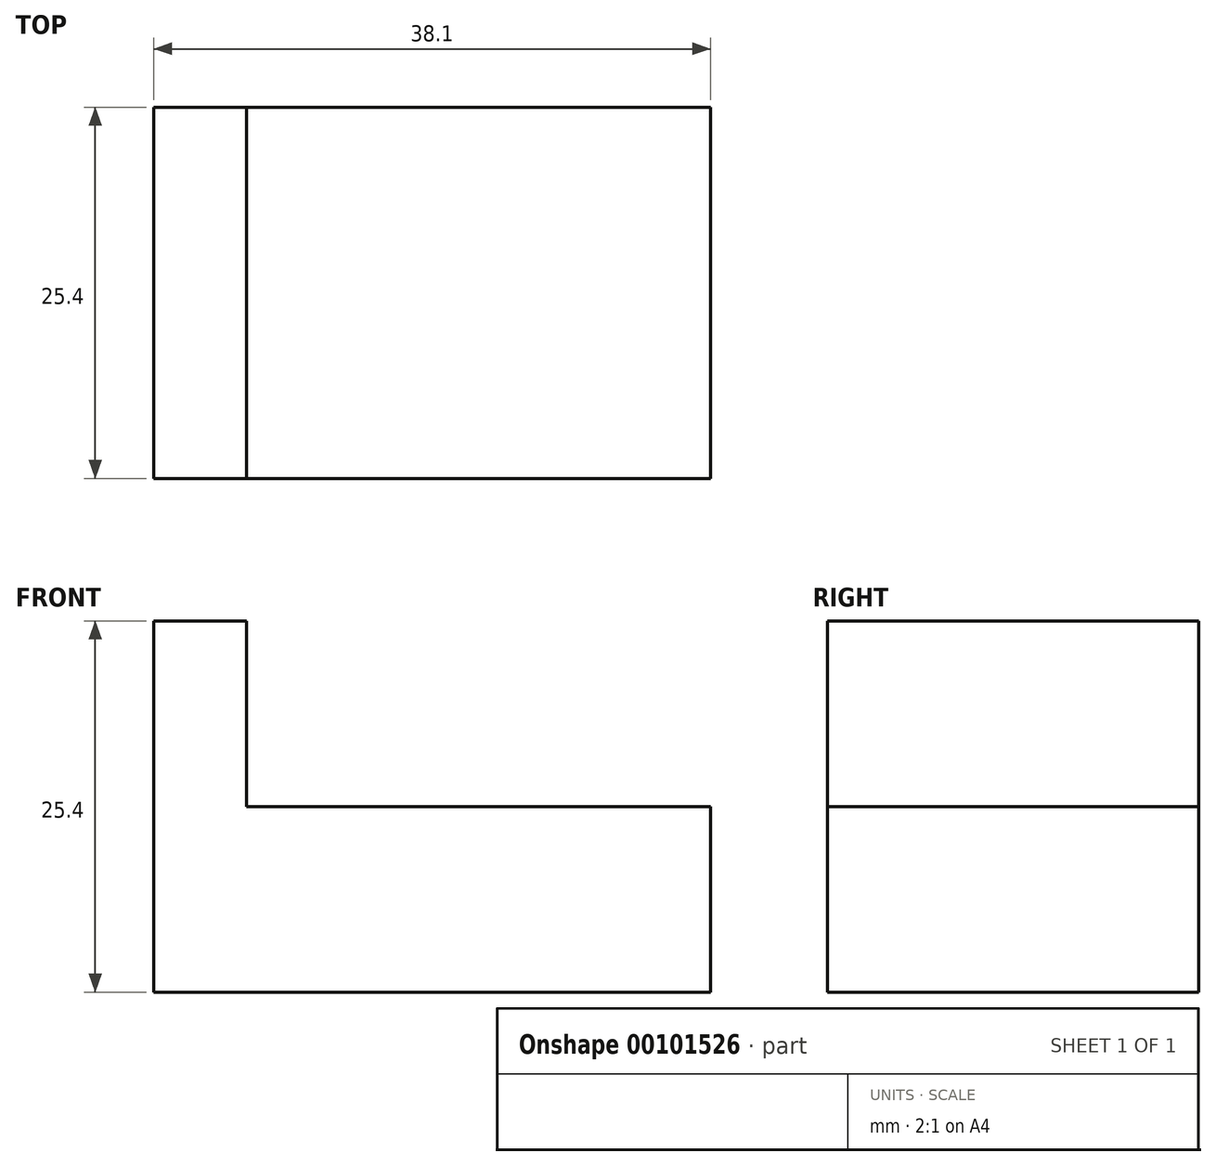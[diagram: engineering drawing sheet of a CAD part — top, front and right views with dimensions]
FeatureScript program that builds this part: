
annotation { "Feature Type Name" : "Feature", "Feature Type Description" : "" }
export const myFeature = defineFeature(function(context is Context, id is Id, definition is map)
    precondition{}
    {
        {
            var Q0;
            Q0=qCreatedBy(makeId("Front.planeOp"),FACE);
            var sketch = newSketch(context, id + "F0", { "sketchPlane" : qUnion([Q0])});
            skLineSegment(sketch, "E0", {"start": v(0, 0) * mm, "end": v(0, 25.4) * mm});
            skLineSegment(sketch, "E1", {"start": v(0, 25.4) * mm, "end": v(6.35, 25.4) * mm});
            skLineSegment(sketch, "E2", {"start": v(6.35, 25.4) * mm, "end": v(6.35, 12.7) * mm});
            skLineSegment(sketch, "E3", {"start": v(6.35, 12.7) * mm, "end": v(38.1, 12.7) * mm});
            skLineSegment(sketch, "E4", {"start": v(38.1, 0) * mm, "end": v(38.1, 12.7) * mm});
            skLineSegment(sketch, "E5", {"start": v(0, 0) * mm, "end": v(38.1, 0) * mm});
            skSolve(sketch);
        }
        {
            var Q0;
            Q0=makeQuery(id+"F0.imprint","IMPRINT",FACE,{"disambiguationData":[TD([[makeQuery(id+"F0.imprint","IMPRINT",EDGE,{"derivedFrom":sQuery(id+"F0.wireOp",EDGE,"E0")}),-1.0]])]});
            extrude(context, id + "F1", {"entities" : qUnion([Q0]), "depth" : 25.4 * mm});
        }
    });
